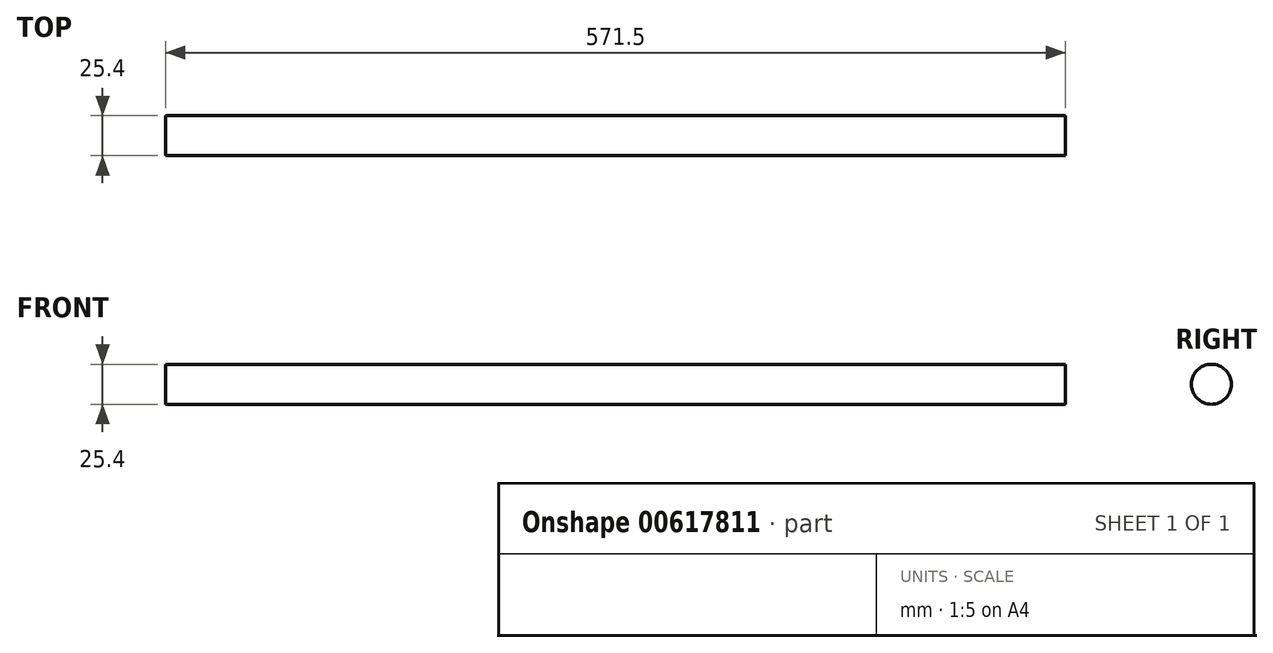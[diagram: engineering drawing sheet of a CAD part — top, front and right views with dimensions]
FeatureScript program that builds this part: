
annotation { "Feature Type Name" : "Feature", "Feature Type Description" : "" }
export const myFeature = defineFeature(function(context is Context, id is Id, definition is map)
    precondition{}
    {
        {
            var Q0;
            Q0=qCreatedBy(makeId("Right.planeOp"),FACE);
            var sketch = newSketch(context, id + "F0", { "sketchPlane" : qUnion([Q0])});
            skCircle(sketch, "E0", {"center": v(0, 0) * mm, "radius": 12.7 * mm});
            skSolve(sketch);
        }
        {
            var Q0;
            Q0=makeQuery(id+"F0.imprint","IMPRINT",FACE,{"disambiguationData":[TD([[makeQuery(id+"F0.imprint","IMPRINT",EDGE,{"derivedFrom":sQuery(id+"F0.wireOp",EDGE,"E0")}),1.0]])]});
            extrude(context, id + "F1", {"entities" : qUnion([Q0]), "depth" : 571.5 * mm, "offsetDistance" : 25.4 * mm});
        }
    });
